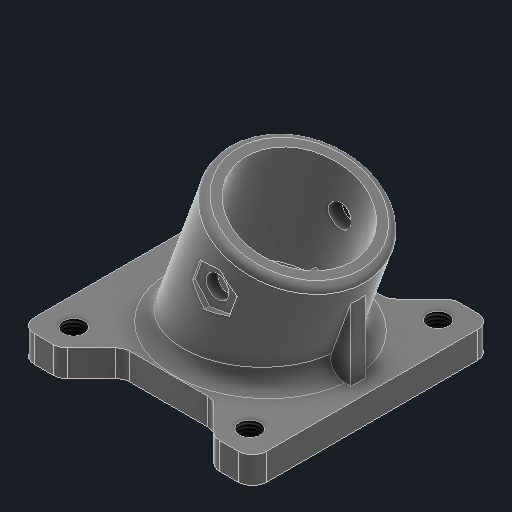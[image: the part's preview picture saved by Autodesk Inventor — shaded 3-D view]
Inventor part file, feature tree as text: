
AUTODESK INVENTOR PART (.ipt)
format: ipt  version: 2024.1 (Build 281209000, 209)  size: 503,296 bytes
history: native  units: mm
features: sketch x11, extrude x10, plane x5, fillet x4, thread x4, projected_geometry x2
ambient origin geometry x8: Origin, YZ Plane, XZ Plane, XY Plane, X Axis, Y Axis, Z Axis, Center Point
bodies: Solid1 (feature_tree)
feature tree (36):
  extrude  "Extrusion1"  Depth=26.8mm
  fillet  "Fillet1"  Radius=3.0mm
  thread  "Thread5"  [1 undecoded]
  thread  "Thread6"  [1 undecoded]
  thread  "Thread7"  [1 undecoded]
  thread  "Thread8"  [1 undecoded]
  plane  "Work Plane2"
  sketch  "Sketch8"  dims[d7=34.0mm d8=5.5mm]
  plane  "Work Plane3"
  extrude  "Extrusion6"  Depth=5.5mm
  extrude  "Extrusion8"  Depth=12.375mm
  extrude  "Extrusion9"  Depth=3.8mm TaperAngle=0.0deg
  extrude  "Extrusion10"  Depth=3.8mm TaperAngle=0.0deg
  fillet  "Fillet4"  Radius=3.8mm
  fillet  "Fillet5"  Radius=3.8mm
  fillet  "Fillet6"  Radius=3.8mm
  extrude  "Extrusion11"  Depth=3.490659mm
  extrude  "Extrusion12"  Depth=16.0mm
  plane  "Work Plane4"
  extrude  "Extrusion13"  Depth=26.5mm TaperAngle=0.0deg
  plane  "Work Plane5"
  plane  "Work Plane6"
  extrude  "Extrusion14"  Depth=1.0mm
  extrude  "Extrusion15"  Depth=17.0mm
  sketch  "Sketch1"  dims[d0=25.0mm d1=26.8mm d2=3.0mm d3=3.0mm d4=3.0mm d5=3.0mm d6=33.0mm]
  projected_geometry  "Projected Loop4"
  sketch  "Sketch9"  dims[d9=5.5mm d10=12.375mm]
  projected_geometry  "Projected Loop5"
  sketch  "Sketch11"  dims[d11=45.0deg d12=3.8mm d13=0.0mm]
  sketch  "Sketch12"  dims[d14=2.0mm d49=3.8mm d50=0.0mm d51=3.8mm d52=0.0mm d53=3.8mm d54=0.0mm d55=3.8mm d56=0.0mm]
  sketch  "Sketch13"  dims[d58=13.4088mm d59=3.490659mm]
  sketch  "Sketch14"  dims[d63=11.0075mm d64=16.0mm]
  sketch  "Sketch15"  dims[d65=20.5mm d66=26.5mm d67=0.0mm]
  sketch  "Sketch16"  dims[d72=17.0mm d73=1.0mm]
  sketch  "Sketch17"  dims[d74=1.0mm d75=17.0mm]
  sketch  "Sketch18"  dims[d76=26.5mm d77=0.0mm d78=30.0mm d79=10.0mm d80=0.0mm d81=0.0mm d82=16.0mm d83=15.0mm d84=0.0mm d85=2.0mm d86=2.0mm d87=1.0mm d88=2.0mm d89=1.0mm d90=5.0mm d91=2.0mm d92=5.0mm d93=13.25mm d94=0.0mm d95=16.0mm d96=12.5mm d97=0.0mm d98=6.25mm d99=3.2mm d100=0.0mm d101=0.0mm d102=10.25mm d103=-10.25mm d104=6.25mm d105=3.2mm d106=1.5mm d107=0.0mm d108=6.25mm d109=12.217305mm d110=6.05mm d111=1.0mm d112=0.0mm]
note: 4 required parameter values undecoded (feature->parameter linkage not recoverable at this tier; creation-order binding heuristic only, values carry confidence <= 0.55)
